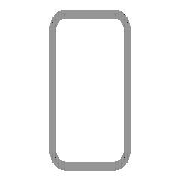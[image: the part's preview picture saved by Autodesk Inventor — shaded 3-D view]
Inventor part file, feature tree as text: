
AUTODESK INVENTOR PART (.ipt)
format: ipt  version: 2025.1 (Build 291241020, 241B)  size: 140,800 bytes
history: native  units: mm (DEFAULTED — no unit token found)
features: other x4, sketch x1, plane x1
ambient origin geometry x8: Origin, YZ Plane, XZ Plane, XY Plane, X Axis, Y Axis, Z Axis, Center Point
bodies: Solid1 (feature_tree), Body (feature_tree)
feature tree (6):
  parser-record x1  (decoder bookkeeping rows leaked as tree rows — omitted from the tree; the rows remain in map.json)
  other  "Driven Length"
  other  "Start Plane"
  other  "End Plane"
  sketch  "Sketch3"  dims[d3=695.833333mm d4=0.0mm d7=6.0mm d9=40.0mm d11=80.0mm d12=3.0mm d13=-0.0mm d14=695.833333mm d15=20.0mm d16=40.0mm d17=90.0deg d18=695.833333mm]
  plane  "Work Plane3"
